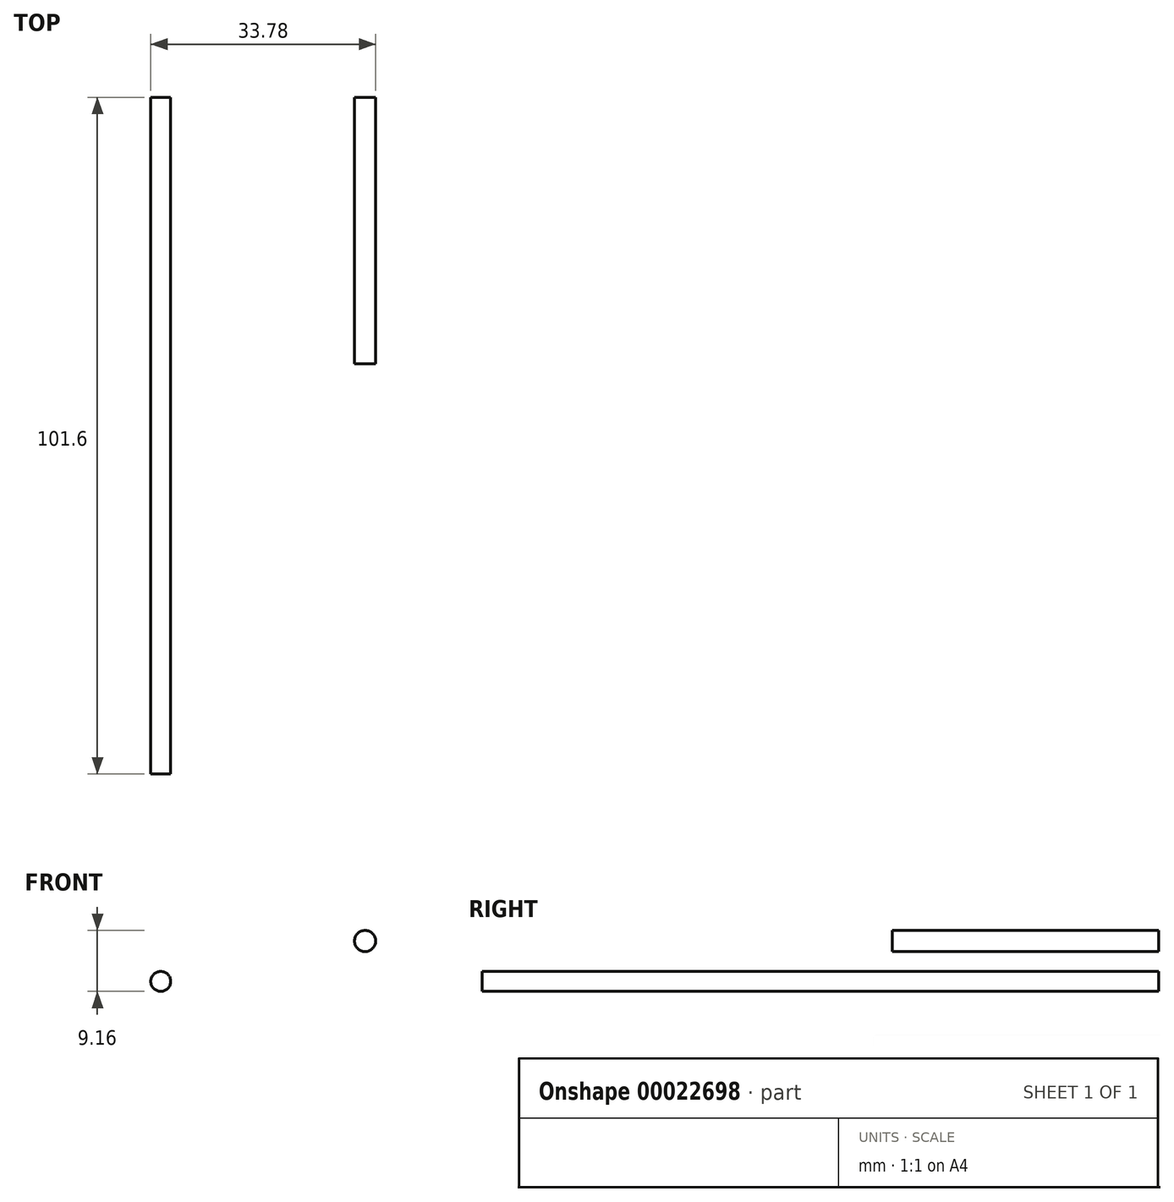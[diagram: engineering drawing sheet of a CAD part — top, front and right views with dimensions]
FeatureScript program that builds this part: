
annotation { "Feature Type Name" : "Feature", "Feature Type Description" : "" }
export const myFeature = defineFeature(function(context is Context, id is Id, definition is map)
    precondition{}
    {
        {
            var Q0;
            Q0=qCreatedBy(makeId("Front.planeOp"),FACE);
            var sketch = newSketch(context, id + "F0", { "sketchPlane" : qUnion([Q0])});
            skCircle(sketch, "E0", {"center": v(-126.14, 33.1) * mm, "radius": 1.5 * mm});
            skSolve(sketch);
        }
        {
            var Q0;
            Q0=makeQuery(id+"F0.imprint","IMPRINT",FACE,{"disambiguationData":[TD([[makeQuery(id+"F0.imprint","IMPRINT",EDGE,{"derivedFrom":sQuery(id+"F0.wireOp",EDGE,"E0")}),1.0]])]});
            var Q1;
            Q1=sQuery(id+"F0.wireOp",EDGE,"E0");
            extrude(context, id + "F1", {"entities" : qUnion([Q0]), "surfaceEntities" : qUnion([Q1]), "depth" : 101.6 * mm});
        }
        {
            var Q0;
            Q0=qCreatedBy(makeId("Front.planeOp"),FACE);
            var sketch = newSketch(context, id + "F2", { "sketchPlane" : qUnion([Q0])});
            skCircle(sketch, "E1", {"center": v(-48.91, 47.52) * mm, "radius": 1.5 * mm});
            skSolve(sketch);
        }
        {
            var Q0;
            Q0=sQuery(id+"F2.wireOp",EDGE,"E1");
            extrude(context, id + "F3", {"bodyType" : ToolBodyType.SURFACE, "surfaceEntities" : qUnion([Q0]), "depth" : 25.4 * mm});
        }
        {
            var Q0;
            Q0=qCreatedBy(makeId("Front.planeOp"),FACE);
            var sketch = newSketch(context, id + "F4", { "sketchPlane" : qUnion([Q0])});
            skCircle(sketch, "E2", {"center": v(-30.38, 43.82) * mm, "radius": 1.5 * mm});
            skSolve(sketch);
        }
        {
            var Q0;
            Q0=sQuery(id+"F4.wireOp",EDGE,"E2");
            extrude(context, id + "F5", {"bodyType" : ToolBodyType.SURFACE, "surfaceEntities" : qUnion([Q0]), "depth" : 25.4 * mm});
        }
        {
            var Q0;
            Q0=qCreatedBy(makeId("Front.planeOp"),FACE);
            var sketch = newSketch(context, id + "F6", { "sketchPlane" : qUnion([Q0])});
            skCircle(sketch, "E3", {"center": v(-95.45, 39.17) * mm, "radius": 1.59 * mm});
            skSolve(sketch);
        }
        {
            var Q0;
            Q0 = qSketchRegion(id + "F6", true);
            var Q1;
            Q1=sQuery(id+"F6.wireOp",EDGE,"E3");
            extrude(context, id + "F7", {"entities" : qUnion([Q0]), "surfaceEntities" : qUnion([Q1]), "depth" : 40 * mm});
        }
    });
